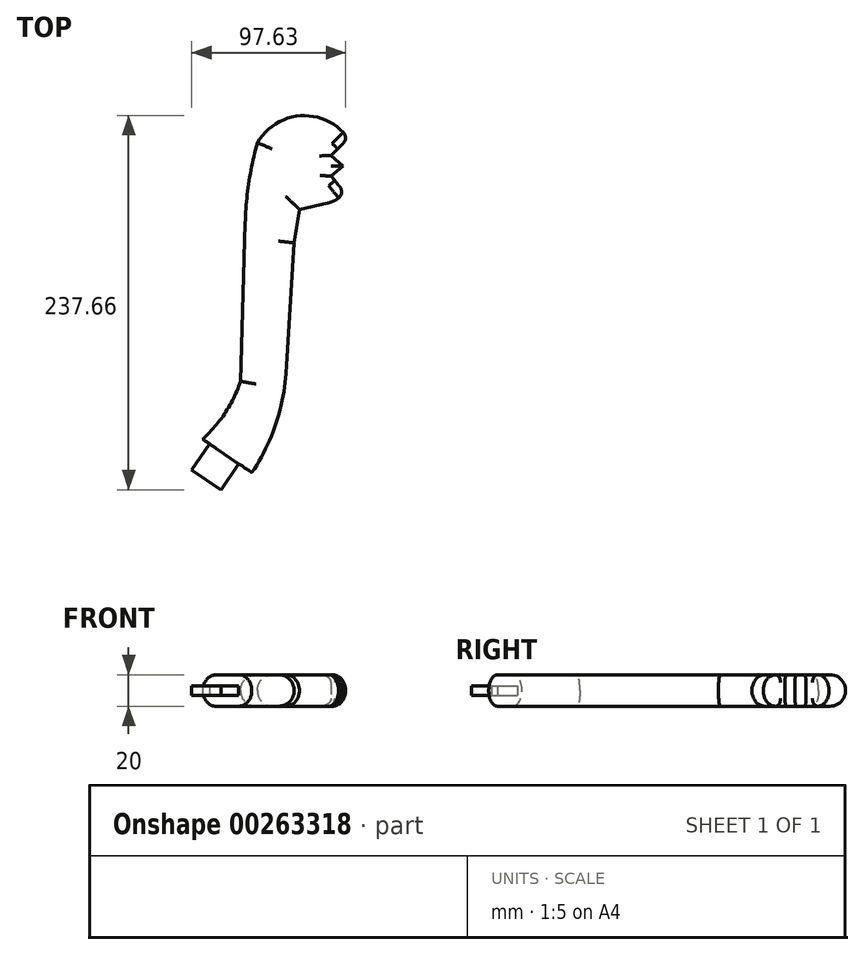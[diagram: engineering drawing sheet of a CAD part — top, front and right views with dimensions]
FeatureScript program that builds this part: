
annotation { "Feature Type Name" : "Feature", "Feature Type Description" : "" }
export const myFeature = defineFeature(function(context is Context, id is Id, definition is map)
    precondition{}
    {
        {
            var Q0;
            Q0=qCreatedBy(makeId("Top.planeOp"),FACE);
            var sketch = newSketch(context, id + "F0", { "sketchPlane" : qUnion([Q0])});
            skArc(sketch, "E0", {"start": v(-69.56, -48.3) * mm, "mid": v(-88.08, -45.25) * mm, "end": v(-106.8, -43.78) * mm});
            skArc(sketch, "E1", {"start": v(-106.8, -43.78) * mm, "mid": v(-96.39, -62.57) * mm, "end": v(-80.73, -77.27) * mm});
            skArc(sketch, "E2", {"start": v(-80.73, -77.27) * mm, "mid": v(-98.26, -84.7) * mm, "end": v(-114.23, -95.07) * mm});
            skArc(sketch, "E3", {"start": v(-114.23, -95.07) * mm, "mid": v(-98.6, -104.41) * mm, "end": v(-80.73, -107.98) * mm});
            skArc(sketch, "E4", {"start": v(-80.73, -107.98) * mm, "mid": v(-90.04, -123.58) * mm, "end": v(-94.69, -141.13) * mm});
            skArc(sketch, "E5", {"start": v(-94.69, -141.13) * mm, "mid": v(-78.8, -139.7) * mm, "end": v(-63.98, -133.8) * mm});
            skArc(sketch, "E6", {"start": v(-63.98, -133.8) * mm, "mid": v(40.14, -139.24) * mm, "end": v(30.94, -35.4) * mm});
            skArc(sketch, "E7", {"start": v(-31.41, -22.87) * mm, "mid": v(-53.17, -31.57) * mm, "end": v(-69.56, -48.3) * mm});
            skCircle(sketch, "E8", {"center": v(-12, -90) * mm, "radius": 35 * mm});
            skLineSegment(sketch, "E9", {"start": v(-12, -90) * mm, "end": v(-12, 0) * mm});
            skLineSegment(sketch, "E10", {"start": v(-12, 0) * mm, "end": v(0, 0) * mm});
            skLineSegment(sketch, "E11", {"start": v(-31.41, -22.87) * mm, "end": v(-12, 0) * mm});
            skLineSegment(sketch, "E12", {"start": v(-31.41, -22.87) * mm, "end": v(0, 0) * mm});
            skArc(sketch, "E13", {"start": v(30.94, -35.4) * mm, "mid": v(57.65, 8.29) * mm, "end": v(64.82, 58.99) * mm});
            skLineSegment(sketch, "E14", {"start": v(64.82, 42.9) * mm, "end": v(70.1, 125.75) * mm});
            skLineSegment(sketch, "E15", {"start": v(70.1, 125.75) * mm, "end": v(73.47, 146.99) * mm});
            skLineSegment(sketch, "E16", {"start": v(73.47, 146.99) * mm, "end": v(91.25, 150.97) * mm});
            skArc(sketch, "E17", {"start": v(93.55, 168.05) * mm, "mid": v(98.13, 170.3) * mm, "end": v(101.04, 174.5) * mm});
            skArc(sketch, "E18", {"start": v(101.04, 174.5) * mm, "mid": v(98.19, 178.86) * mm, "end": v(93.55, 181.22) * mm});
            skArc(sketch, "E19", {"start": v(91.25, 150.97) * mm, "mid": v(97.19, 153.5) * mm, "end": v(101.85, 157.96) * mm});
            skArc(sketch, "E20", {"start": v(101.85, 157.96) * mm, "mid": v(99.5, 164.5) * mm, "end": v(93.55, 168.05) * mm});
            skArc(sketch, "E21", {"start": v(93.55, 181.22) * mm, "mid": v(100.45, 185.24) * mm, "end": v(104.38, 192.2) * mm});
            skArc(sketch, "E22", {"start": v(16.27, 5.35) * mm, "mid": v(27.94, 20.47) * mm, "end": v(35.96, 37.8) * mm});
            skLineSegment(sketch, "E23", {"start": v(16.27, 5.35) * mm, "end": v(12.02, 0.97) * mm});
            skLineSegment(sketch, "E24", {"start": v(12.02, 54.47) * mm, "end": v(16.98, 220.58) * mm});
            skLineSegment(sketch, "E25", {"start": v(16.98, 220.58) * mm, "end": v(16.98, 230.48) * mm});
            skArc(sketch, "E26", {"start": v(20.74, 234.78) * mm, "mid": v(18.05, 233.34) * mm, "end": v(16.98, 230.48) * mm});
            skLineSegment(sketch, "E27", {"start": v(20.74, 234.78) * mm, "end": v(55.67, 234.78) * mm});
            skArc(sketch, "E28", {"start": v(55.67, 234.78) * mm, "mid": v(75.45, 242.82) * mm, "end": v(84, 262.38) * mm});
            skArc(sketch, "E29", {"start": v(84, 262.38) * mm, "mid": v(83.8, 275) * mm, "end": v(79.59, 286.9) * mm});
            skArc(sketch, "E30", {"start": v(79.59, 286.9) * mm, "mid": v(90.12, 305.47) * mm, "end": v(96.46, 325.87) * mm});
            skArc(sketch, "E31", {"start": v(96.46, 325.87) * mm, "mid": v(80.34, 314.22) * mm, "end": v(65.52, 300.95) * mm});
            skArc(sketch, "E32", {"start": v(65.52, 300.95) * mm, "mid": v(66.02, 314.82) * mm, "end": v(65.52, 328.68) * mm});
            skArc(sketch, "E33", {"start": v(41.86, 304.54) * mm, "mid": v(40.03, 315.53) * mm, "end": v(35.9, 325.87) * mm});
            skArc(sketch, "E34", {"start": v(35.9, 325.87) * mm, "mid": v(29.68, 316.4) * mm, "end": v(23.68, 306.81) * mm});
            skArc(sketch, "E35", {"start": v(23.68, 306.81) * mm, "mid": v(-21.12, 284.92) * mm, "end": v(-28, 235.53) * mm});
            skLineSegment(sketch, "E36", {"start": v(-31.41, -22.87) * mm, "end": v(-28, 235.53) * mm});
            skLineSegment(sketch, "E37", {"start": v(0, 0) * mm, "end": v(0, 302.13) * mm});
            skLineSegment(sketch, "E38", {"start": v(12.02, 0.97) * mm, "end": v(-31.41, -22.87) * mm});
            skLineSegment(sketch, "E39", {"start": v(0, 0) * mm, "end": v(12.02, 0.97) * mm});
            skLineSegment(sketch, "E40", {"start": v(12.02, 0.97) * mm, "end": v(30.94, -35.4) * mm});
            skLineSegment(sketch, "E41", {"start": v(64.82, 58.99) * mm, "end": v(46.6, 104.17) * mm});
            skLineSegment(sketch, "E42", {"start": v(12.02, 0.97) * mm, "end": v(12.02, 54.47) * mm});
            skLineSegment(sketch, "E43", {"start": v(-29.54, 119.27) * mm, "end": v(13.94, 118.7) * mm});
            skLineSegment(sketch, "E44", {"start": v(35.96, 37.8) * mm, "end": v(38.97, 138.47) * mm});
            skArc(sketch, "E45", {"start": v(104.38, 192.2) * mm, "mid": v(74.78, 206.52) * mm, "end": v(46.71, 189.39) * mm});
            skArc(sketch, "E46", {"start": v(46.71, 189.39) * mm, "mid": v(41.3, 164.16) * mm, "end": v(38.97, 138.47) * mm});
            skLineSegment(sketch, "E47", {"start": v(104.38, 192.2) * mm, "end": v(93.55, 181.22) * mm});
            skLineSegment(sketch, "E48", {"start": v(93.55, 168.05) * mm, "end": v(101.85, 157.96) * mm});
            skLineSegment(sketch, "E49", {"start": v(93.55, 181.22) * mm, "end": v(101.04, 174.5) * mm});
            skLineSegment(sketch, "E50", {"start": v(93.55, 168.05) * mm, "end": v(101.04, 174.5) * mm});
            skLineSegment(sketch, "E51", {"start": v(41.86, 304.54) * mm, "end": v(65.52, 328.68) * mm});
            skLineSegment(sketch, "E52", {"start": v(16.98, 230.48) * mm, "end": v(-28.07, 230.48) * mm});
            skLineSegment(sketch, "E53", {"start": v(12.02, 0.97) * mm, "end": v(-31.1, 0.49) * mm});
            skPoint(sketch, "E53.endSnap0", {"position": v(6.01, 0.49) * mm});
            skLineSegment(sketch, "E54", {"start": v(12.02, 0.97) * mm, "end": v(43.15, -20.17) * mm});
            skSolve(sketch);
        }
        {
            var Q0;
            {var subQ0=sQuery(id+"F0.wireOp",EDGE,"E38");var subQ1=sQuery(id+"F0.wireOp",EDGE,"E9");var subQ2=makeQuery(id+"F0.imprint","INTERSECT",VERTEX,{"derivedFrom":[subQ1,subQ0]});Q0=makeQuery(id+"F0.imprint","IMPRINT",FACE,{"disambiguationData":[TD([[makeQuery(id+"F0.imprint","IMPRINT",EDGE,{"disambiguationData":[TD([[subQ2,-1.0]])],"derivedFrom":subQ1}),1.0]])]});}
            var Q1;
            {var subQ0=sQuery(id+"F0.wireOp",EDGE,"E11");Q1=makeQuery(id+"F0.imprint","IMPRINT",FACE,{"disambiguationData":[TD([[makeQuery(id+"F0.imprint","IMPRINT",EDGE,{"derivedFrom":subQ0}),-1.0]])]});}
            var Q2;
            {var subQ0=sQuery(id+"F0.wireOp",EDGE,"E39");Q2=makeQuery(id+"F0.imprint","IMPRINT",FACE,{"disambiguationData":[TD([[makeQuery(id+"F0.imprint","IMPRINT",EDGE,{"derivedFrom":subQ0}),1.0]])]});}
            var Q3;
            Q3=makeQuery(id+"F0.imprint","IMPRINT",FACE,{"disambiguationData":[TD([[makeQuery(id+"F0.imprint","IMPRINT",EDGE,{"derivedFrom":sQuery(id+"F0.wireOp",EDGE,"E0")}),1.0]])]});
            var Q4;
            {var subQ5=sQuery(id+"F0.wireOp",EDGE,"E39");Q4=makeQuery(id+"F0.imprint","IMPRINT",FACE,{"disambiguationData":[TD([[makeQuery(id+"F0.imprint","IMPRINT",EDGE,{"derivedFrom":subQ5}),-1.0]])]});}
            var Q5;
            {var subQ2=sQuery(id+"F0.wireOp",EDGE,"E10");Q5=makeQuery(id+"F0.imprint","IMPRINT",FACE,{"disambiguationData":[TD([[makeQuery(id+"F0.imprint","IMPRINT",EDGE,{"derivedFrom":subQ2}),1.0]])]});}
            var Q6;
            {var subQ0=sQuery(id+"F0.wireOp",EDGE,"E10");Q6=makeQuery(id+"F0.imprint","IMPRINT",FACE,{"disambiguationData":[TD([[makeQuery(id+"F0.imprint","IMPRINT",EDGE,{"derivedFrom":subQ0}),-1.0]])]});}
            var Q7;
            {var subQ0=sQuery(id+"F0.wireOp",EDGE,"E40");Q7=makeQuery(id+"F0.imprint","IMPRINT",FACE,{"disambiguationData":[TD([[makeQuery(id+"F0.imprint","IMPRINT",EDGE,{"derivedFrom":subQ0}),1.0]])]});}
            extrude(context, id + "F1", {"entities" : qUnion([Q0, Q1, Q2, Q3, Q4, Q5, Q6, Q7]), "depth" : 20 * mm});
        }
        {
            var Q0;
            {var subQ1=sQuery(id+"F0.wireOp",EDGE,"E14");Q0=makeQuery(id+"F0.imprint","IMPRINT",FACE,{"disambiguationData":[TD([[makeQuery(id+"F0.imprint","IMPRINT",EDGE,{"derivedFrom":subQ1}),1.0]])]});}
            extrude(context, id + "F2", {"entities" : qUnion([Q0]), "depth" : 20 * mm});
        }
        {
            var Q0;
            {var subQ0=sQuery(id+"F0.wireOp",EDGE,"E43");var subQ1=sQuery(id+"F0.wireOp",EDGE,"E36");var subQ2=makeQuery(id+"F0.imprint","INTERSECT",VERTEX,{"derivedFrom":[subQ1,subQ0]});Q0=makeQuery(id+"F0.imprint","IMPRINT",FACE,{"disambiguationData":[TD([[makeQuery(id+"F0.imprint","IMPRINT",EDGE,{"disambiguationData":[TD([[subQ2,1.0]])],"derivedFrom":subQ1}),-1.0]])]});}
            var Q1;
            {var subQ5=sQuery(id+"F0.wireOp",EDGE,"E42");Q1=makeQuery(id+"F0.imprint","IMPRINT",FACE,{"disambiguationData":[TD([[makeQuery(id+"F0.imprint","IMPRINT",EDGE,{"derivedFrom":subQ5}),1.0]])]});}
            var Q2;
            {var subQ0=sQuery(id+"F0.wireOp",EDGE,"E43");var subQ1=sQuery(id+"F0.wireOp",EDGE,"E36");var subQ2=makeQuery(id+"F0.imprint","INTERSECT",VERTEX,{"derivedFrom":[subQ1,subQ0]});Q2=makeQuery(id+"F0.imprint","IMPRINT",FACE,{"disambiguationData":[TD([[makeQuery(id+"F0.imprint","IMPRINT",EDGE,{"disambiguationData":[TD([[subQ2,-1.0]])],"derivedFrom":subQ1}),-1.0]])]});}
            var Q3;
            {var subQ7=sQuery(id+"F0.wireOp",EDGE,"E25");Q3=makeQuery(id+"F0.imprint","IMPRINT",FACE,{"disambiguationData":[TD([[makeQuery(id+"F0.imprint","IMPRINT",EDGE,{"derivedFrom":subQ7}),1.0]])]});}
            extrude(context, id + "F3", {"entities" : qUnion([Q0, Q1, Q2, Q3]), "depth" : 20 * mm});
        }
        {
            var Q0;
            {var subQ0=sQuery(id+"F0.wireOp",EDGE,"E36");var subQ1=sQuery(id+"F0.wireOp",EDGE,"E35");var subQ2=makeQuery(id+"F0.imprint","INTERSECT",VERTEX,{"derivedFrom":[subQ1,subQ0]});Q0=makeQuery(id+"F0.imprint","IMPRINT",FACE,{"disambiguationData":[TD([[makeQuery(id+"F0.imprint","IMPRINT",EDGE,{"disambiguationData":[TD([[subQ2,1.0]])],"derivedFrom":subQ1}),1.0]])]});}
            var Q1;
            {var subQ4=sQuery(id+"F0.wireOp",EDGE,"E26");Q1=makeQuery(id+"F0.imprint","IMPRINT",FACE,{"disambiguationData":[TD([[makeQuery(id+"F0.imprint","IMPRINT",EDGE,{"derivedFrom":subQ4}),-1.0]])]});}
            extrude(context, id + "F4", {"entities" : qUnion([Q0, Q1]), "depth" : 20 * mm});
        }
        {
            var Q0;
            Q0=makeQuery(id+"F1.opExtrude","CAP_EDGE",EDGE,{"disambiguationData":[OSD([sQuery(id+"F0.wireOp",EDGE,"E36")])],"isStart":false});
            var Q1;
            Q1=makeQuery(id+"F1.opExtrude","CAP_EDGE",EDGE,{"disambiguationData":[OSD([sQuery(id+"F0.wireOp",EDGE,"E24")])],"isStart":false});
            var Q2;
            Q2=makeQuery(id+"F1.opExtrude","CAP_EDGE",EDGE,{"disambiguationData":[OSD([sQuery(id+"F0.wireOp",EDGE,"E42")])],"isStart":false});
            var Q3;
            Q3=makeQuery(id+"F1.opExtrude","CAP_EDGE",EDGE,{"disambiguationData":[OSD([sQuery(id+"F0.wireOp",EDGE,"E25")])],"isStart":false});
            var Q4;
            Q4=makeQuery(id+"F1.opExtrude","CAP_EDGE",EDGE,{"disambiguationData":[OSD([sQuery(id+"F0.wireOp",EDGE,"E35")])],"isStart":false});
            var Q5;
            Q5=makeQuery(id+"F1.opExtrude","CAP_EDGE",EDGE,{"disambiguationData":[OSD([sQuery(id+"F0.wireOp",EDGE,"E26")])],"isStart":false});
            var Q6;
            Q6=makeQuery(id+"F1.opExtrude","CAP_EDGE",EDGE,{"disambiguationData":[OSD([sQuery(id+"F0.wireOp",EDGE,"E42")])],"isStart":true});
            var Q7;
            Q7=makeQuery(id+"F1.opExtrude","CAP_EDGE",EDGE,{"disambiguationData":[OSD([sQuery(id+"F0.wireOp",EDGE,"E25")])],"isStart":true});
            var Q8;
            Q8=makeQuery(id+"F1.opExtrude","CAP_EDGE",EDGE,{"disambiguationData":[OSD([sQuery(id+"F0.wireOp",EDGE,"E36")])],"isStart":true});
            var Q9;
            Q9=makeQuery(id+"F1.opExtrude","CAP_EDGE",EDGE,{"disambiguationData":[OSD([sQuery(id+"F0.wireOp",EDGE,"E35")])],"isStart":true});
            var Q10;
            Q10=makeQuery(id+"F1.opExtrude","CAP_EDGE",EDGE,{"disambiguationData":[OSD([sQuery(id+"F0.wireOp",EDGE,"E26")])],"isStart":true});
            var Q11;
            Q11=makeQuery(id+"F1.opExtrude","CAP_EDGE",EDGE,{"disambiguationData":[OSD([sQuery(id+"F0.wireOp",EDGE,"E22")])],"isStart":false});
            var Q12;
            Q12=makeQuery(id+"F1.opExtrude","CAP_EDGE",EDGE,{"disambiguationData":[OSD([sQuery(id+"F0.wireOp",EDGE,"E23")])],"isStart":false});
            var Q13;
            Q13=makeQuery(id+"F1.opExtrude","CAP_EDGE",EDGE,{"disambiguationData":[OSD([sQuery(id+"F0.wireOp",EDGE,"E44")])],"isStart":false});
            var Q14;
            Q14=makeQuery(id+"F1.opExtrude","CAP_EDGE",EDGE,{"disambiguationData":[OSD([sQuery(id+"F0.wireOp",EDGE,"E45")])],"isStart":false});
            var Q15;
            Q15=makeQuery(id+"F1.opExtrude","CAP_EDGE",EDGE,{"disambiguationData":[OSD([sQuery(id+"F0.wireOp",EDGE,"E22")])],"isStart":true});
            var Q16;
            Q16=makeQuery(id+"F1.opExtrude","CAP_EDGE",EDGE,{"disambiguationData":[OSD([sQuery(id+"F0.wireOp",EDGE,"E44")])],"isStart":true});
            var Q17;
            Q17=makeQuery(id+"F1.opExtrude","CAP_EDGE",EDGE,{"disambiguationData":[OSD([sQuery(id+"F0.wireOp",EDGE,"E45")])],"isStart":true});
            var Q18;
            Q18=makeQuery(id+"F1.opExtrude","CAP_EDGE",EDGE,{"disambiguationData":[OSD([sQuery(id+"F0.wireOp",EDGE,"E13")])],"isStart":false});
            var Q19;
            Q19=makeQuery(id+"F1.opExtrude","CAP_EDGE",EDGE,{"disambiguationData":[OSD([sQuery(id+"F0.wireOp",EDGE,"E14")])],"isStart":false});
            var Q20;
            Q20=makeQuery(id+"F1.opExtrude","CAP_EDGE",EDGE,{"disambiguationData":[OSD([sQuery(id+"F0.wireOp",EDGE,"E15")])],"isStart":false});
            var Q21;
            Q21=makeQuery(id+"F1.opExtrude","CAP_EDGE",EDGE,{"disambiguationData":[OSD([sQuery(id+"F0.wireOp",EDGE,"E16")])],"isStart":false});
            var Q22;
            Q22=makeQuery(id+"F1.opExtrude","CAP_EDGE",EDGE,{"disambiguationData":[OSD([sQuery(id+"F0.wireOp",EDGE,"E16")])],"isStart":true});
            var Q23;
            Q23=makeQuery(id+"F1.opExtrude","CAP_EDGE",EDGE,{"disambiguationData":[OSD([sQuery(id+"F0.wireOp",EDGE,"E15")])],"isStart":true});
            var Q24;
            Q24=makeQuery(id+"F1.opExtrude","CAP_EDGE",EDGE,{"disambiguationData":[OSD([sQuery(id+"F0.wireOp",EDGE,"E14")])],"isStart":true});
            var Q25;
            Q25=makeQuery(id+"F1.opExtrude","CAP_EDGE",EDGE,{"disambiguationData":[OSD([sQuery(id+"F0.wireOp",EDGE,"E13")])],"isStart":true});
            var Q26;
            Q26=makeQuery(id+"F1.opExtrude","CAP_EDGE",EDGE,{"disambiguationData":[OSD([sQuery(id+"F0.wireOp",EDGE,"E6")])],"isStart":false});
            var Q27;
            Q27=makeQuery(id+"F1.opExtrude","CAP_EDGE",EDGE,{"disambiguationData":[OSD([sQuery(id+"F0.wireOp",EDGE,"E8")])],"isStart":false});
            var Q28;
            Q28=makeQuery(id+"F1.opExtrude","CAP_EDGE",EDGE,{"disambiguationData":[OSD([sQuery(id+"F0.wireOp",EDGE,"E7")])],"isStart":false});
            var Q29;
            Q29=makeQuery(id+"F1.opExtrude","CAP_EDGE",EDGE,{"disambiguationData":[OSD([sQuery(id+"F0.wireOp",EDGE,"E8")])],"isStart":true});
            var Q30;
            Q30=makeQuery(id+"F1.opExtrude","CAP_EDGE",EDGE,{"disambiguationData":[OSD([sQuery(id+"F0.wireOp",EDGE,"E7")])],"isStart":true});
            var Q31;
            Q31=makeQuery(id+"F1.opExtrude","CAP_EDGE",EDGE,{"disambiguationData":[OSD([sQuery(id+"F0.wireOp",EDGE,"E6")])],"isStart":true});
            fillet(context, id + "F5", {"entities" : qUnion([Q0, Q1, Q2, Q3, Q4, Q5, Q6, Q7, Q8, Q9, Q10, Q11, Q12, Q13, Q14, Q15, Q16, Q17, Q18, Q19, Q20, Q21, Q22, Q23, Q24, Q25, Q26, Q27, Q28, Q29, Q30, Q31]), "radius" : 10 * mm, "tangentPropagation" : true, "allowEdgeOverflow" : false});
        }
        {
            var Q0;
            Q0=makeQuery(id+"F1.opExtrude","CAP_EDGE",EDGE,{"disambiguationData":[OSD([sQuery(id+"F0.wireOp",EDGE,"E0")])],"isStart":false});
            var Q1;
            Q1=makeQuery(id+"F1.opExtrude","CAP_EDGE",EDGE,{"disambiguationData":[OSD([sQuery(id+"F0.wireOp",EDGE,"E1")])],"isStart":false});
            var Q2;
            Q2=makeQuery(id+"F1.opExtrude","CAP_EDGE",EDGE,{"disambiguationData":[OSD([sQuery(id+"F0.wireOp",EDGE,"E5")])],"isStart":false});
            var Q3;
            Q3=makeQuery(id+"F1.opExtrude","CAP_EDGE",EDGE,{"disambiguationData":[OSD([sQuery(id+"F0.wireOp",EDGE,"E4")])],"isStart":false});
            var Q4;
            Q4=makeQuery(id+"F1.opExtrude","CAP_EDGE",EDGE,{"disambiguationData":[OSD([sQuery(id+"F0.wireOp",EDGE,"E0")])],"isStart":true});
            var Q5;
            Q5=makeQuery(id+"F1.opExtrude","CAP_EDGE",EDGE,{"disambiguationData":[OSD([sQuery(id+"F0.wireOp",EDGE,"E1")])],"isStart":true});
            var Q6;
            Q6=makeQuery(id+"F1.opExtrude","CAP_EDGE",EDGE,{"disambiguationData":[OSD([sQuery(id+"F0.wireOp",EDGE,"E4")])],"isStart":true});
            var Q7;
            Q7=makeQuery(id+"F1.opExtrude","CAP_EDGE",EDGE,{"disambiguationData":[OSD([sQuery(id+"F0.wireOp",EDGE,"E5")])],"isStart":true});
            fillet(context, id + "F6", {"entities" : qUnion([Q0, Q1, Q2, Q3, Q4, Q5, Q6, Q7]), "radius" : 9.5 * mm, "tangentPropagation" : true, "rho" : 0.5, "crossSection" : FilletCrossSection.CONIC, "allowEdgeOverflow" : false});
        }
        {
            var Q0;
            Q0=makeQuery(id+"F1.opExtrude","CAP_EDGE",EDGE,{"disambiguationData":[OSD([sQuery(id+"F0.wireOp",EDGE,"E3")])],"isStart":true});
            var Q1;
            Q1=makeQuery(id+"F1.opExtrude","CAP_EDGE",EDGE,{"disambiguationData":[OSD([sQuery(id+"F0.wireOp",EDGE,"E2")])],"isStart":true});
            var Q2;
            Q2=makeQuery(id+"F1.opExtrude","CAP_EDGE",EDGE,{"disambiguationData":[OSD([sQuery(id+"F0.wireOp",EDGE,"E2")])],"isStart":false});
            var Q3;
            Q3=makeQuery(id+"F1.opExtrude","CAP_EDGE",EDGE,{"disambiguationData":[OSD([sQuery(id+"F0.wireOp",EDGE,"E3")])],"isStart":false});
            fillet(context, id + "F7", {"entities" : qUnion([Q0, Q1, Q2, Q3]), "radius" : 3 * mm, "tangentPropagation" : true, "allowEdgeOverflow" : false});
        }
        {
            var Q0;
            Q0=makeQuery(id+"F2.opExtrude","CAP_EDGE",EDGE,{"disambiguationData":[OSD([sQuery(id+"F0.wireOp",EDGE,"E14")])],"isStart":false});
            var Q1;
            Q1=makeQuery(id+"F2.opExtrude","CAP_EDGE",EDGE,{"disambiguationData":[OSD([sQuery(id+"F0.wireOp",EDGE,"E15")])],"isStart":false});
            var Q2;
            Q2=makeQuery(id+"F2.opExtrude","CAP_EDGE",EDGE,{"disambiguationData":[OSD([sQuery(id+"F0.wireOp",EDGE,"E14")])],"isStart":true});
            var Q3;
            Q3=makeQuery(id+"F2.opExtrude","CAP_EDGE",EDGE,{"disambiguationData":[OSD([sQuery(id+"F0.wireOp",EDGE,"E15")])],"isStart":true});
            var Q4;
            Q4=makeQuery(id+"F2.opExtrude","CAP_EDGE",EDGE,{"disambiguationData":[OSD([sQuery(id+"F0.wireOp",EDGE,"E16")])],"isStart":true});
            var Q5;
            Q5=makeQuery(id+"F2.opExtrude","CAP_EDGE",EDGE,{"disambiguationData":[OSD([sQuery(id+"F0.wireOp",EDGE,"E16")])],"isStart":false});
            var Q6;
            Q6=makeQuery(id+"F2.opExtrude","CAP_EDGE",EDGE,{"disambiguationData":[OSD([sQuery(id+"F0.wireOp",EDGE,"E45")])],"isStart":true});
            var Q7;
            Q7=makeQuery(id+"F2.opExtrude","CAP_EDGE",EDGE,{"disambiguationData":[OSD([sQuery(id+"F0.wireOp",EDGE,"E45")])],"isStart":false});
            var Q8;
            Q8=makeQuery(id+"F2.opExtrude","CAP_EDGE",EDGE,{"disambiguationData":[OSD([sQuery(id+"F0.wireOp",EDGE,"E46")])],"isStart":false});
            var Q9;
            Q9=makeQuery(id+"F2.opExtrude","CAP_EDGE",EDGE,{"disambiguationData":[OSD([sQuery(id+"F0.wireOp",EDGE,"E44")])],"isStart":false});
            var Q10;
            Q10=makeQuery(id+"F2.opExtrude","CAP_EDGE",EDGE,{"disambiguationData":[OSD([sQuery(id+"F0.wireOp",EDGE,"E22")])],"isStart":false});
            var Q11;
            Q11=makeQuery(id+"F2.opExtrude","CAP_EDGE",EDGE,{"disambiguationData":[OSD([sQuery(id+"F0.wireOp",EDGE,"E23")])],"isStart":false});
            var Q12;
            Q12=makeQuery(id+"F2.opExtrude","CAP_EDGE",EDGE,{"disambiguationData":[OSD([sQuery(id+"F0.wireOp",EDGE,"E46")])],"isStart":true});
            var Q13;
            Q13=makeQuery(id+"F2.opExtrude","CAP_EDGE",EDGE,{"disambiguationData":[OSD([sQuery(id+"F0.wireOp",EDGE,"E23")])],"isStart":true});
            var Q14;
            Q14=makeQuery(id+"F2.opExtrude","CAP_EDGE",EDGE,{"disambiguationData":[OSD([sQuery(id+"F0.wireOp",EDGE,"E22")])],"isStart":true});
            var Q15;
            Q15=makeQuery(id+"F2.opExtrude","CAP_EDGE",EDGE,{"disambiguationData":[OSD([sQuery(id+"F0.wireOp",EDGE,"E44")])],"isStart":true});
            var Q16;
            Q16=makeQuery(id+"F3.opExtrude","CAP_EDGE",EDGE,{"disambiguationData":[OSD([sQuery(id+"F0.wireOp",EDGE,"E24")])],"isStart":false});
            var Q17;
            Q17=makeQuery(id+"F3.opExtrude","CAP_EDGE",EDGE,{"disambiguationData":[OSD([sQuery(id+"F0.wireOp",EDGE,"E42")])],"isStart":false});
            var Q18;
            Q18=makeQuery(id+"F3.opExtrude","CAP_EDGE",EDGE,{"disambiguationData":[OSD([sQuery(id+"F0.wireOp",EDGE,"E42")])],"isStart":true});
            var Q19;
            Q19=makeQuery(id+"F3.opExtrude","CAP_EDGE",EDGE,{"disambiguationData":[OSD([sQuery(id+"F0.wireOp",EDGE,"E24")])],"isStart":true});
            var Q20;
            Q20=makeQuery(id+"F3.opExtrude","CAP_EDGE",EDGE,{"disambiguationData":[OSD([sQuery(id+"F0.wireOp",EDGE,"E25")])],"isStart":true});
            var Q21;
            Q21=makeQuery(id+"F3.opExtrude","CAP_EDGE",EDGE,{"disambiguationData":[OSD([sQuery(id+"F0.wireOp",EDGE,"E36")])],"isStart":false});
            var Q22;
            Q22=makeQuery(id+"F3.opExtrude","CAP_EDGE",EDGE,{"disambiguationData":[OSD([sQuery(id+"F0.wireOp",EDGE,"E36")])],"isStart":true});
            var Q23;
            Q23=makeQuery(id+"F4.opExtrude","CAP_EDGE",EDGE,{"disambiguationData":[OSD([sQuery(id+"F0.wireOp",EDGE,"E36")])],"isStart":true});
            var Q24;
            Q24=makeQuery(id+"F4.opExtrude","CAP_EDGE",EDGE,{"disambiguationData":[OSD([sQuery(id+"F0.wireOp",EDGE,"E36")])],"isStart":false});
            var Q25;
            Q25=makeQuery(id+"F4.opExtrude","CAP_EDGE",EDGE,{"disambiguationData":[OSD([sQuery(id+"F0.wireOp",EDGE,"E35")])],"isStart":true});
            var Q26;
            Q26=makeQuery(id+"F4.opExtrude","CAP_EDGE",EDGE,{"disambiguationData":[OSD([sQuery(id+"F0.wireOp",EDGE,"E35")])],"isStart":false});
            var Q27;
            Q27=makeQuery(id+"F4.opExtrude","CAP_EDGE",EDGE,{"disambiguationData":[OSD([sQuery(id+"F0.wireOp",EDGE,"E27")])],"isStart":false});
            var Q28;
            Q28=makeQuery(id+"F4.opExtrude","CAP_EDGE",EDGE,{"disambiguationData":[OSD([sQuery(id+"F0.wireOp",EDGE,"E28")])],"isStart":false});
            var Q29;
            Q29=makeQuery(id+"F4.opExtrude","CAP_EDGE",EDGE,{"disambiguationData":[OSD([sQuery(id+"F0.wireOp",EDGE,"E29")])],"isStart":false});
            var Q30;
            Q30=makeQuery(id+"F4.opExtrude","CAP_EDGE",EDGE,{"disambiguationData":[OSD([sQuery(id+"F0.wireOp",EDGE,"E27")])],"isStart":true});
            var Q31;
            Q31=makeQuery(id+"F4.opExtrude","CAP_EDGE",EDGE,{"disambiguationData":[OSD([sQuery(id+"F0.wireOp",EDGE,"E28")])],"isStart":true});
            var Q32;
            Q32=makeQuery(id+"F4.opExtrude","CAP_EDGE",EDGE,{"disambiguationData":[OSD([sQuery(id+"F0.wireOp",EDGE,"E29")])],"isStart":true});
            var Q33;
            Q33=makeQuery(id+"F4.opExtrude","CAP_EDGE",EDGE,{"disambiguationData":[OSD([sQuery(id+"F0.wireOp",EDGE,"E26")])],"isStart":false});
            var Q34;
            Q34=makeQuery(id+"F4.opExtrude","CAP_EDGE",EDGE,{"disambiguationData":[OSD([sQuery(id+"F0.wireOp",EDGE,"E26")])],"isStart":true});
            var Q35;
            Q35=makeQuery(id+"F4.opExtrude","CAP_EDGE",EDGE,{"disambiguationData":[OSD([sQuery(id+"F0.wireOp",EDGE,"E30")])],"isStart":false});
            var Q36;
            Q36=makeQuery(id+"F4.opExtrude","CAP_EDGE",EDGE,{"disambiguationData":[OSD([sQuery(id+"F0.wireOp",EDGE,"E31")])],"isStart":false});
            var Q37;
            Q37=makeQuery(id+"F4.opExtrude","CAP_EDGE",EDGE,{"disambiguationData":[OSD([sQuery(id+"F0.wireOp",EDGE,"E30")])],"isStart":true});
            var Q38;
            Q38=makeQuery(id+"F4.opExtrude","CAP_EDGE",EDGE,{"disambiguationData":[OSD([sQuery(id+"F0.wireOp",EDGE,"E31")])],"isStart":true});
            var Q39;
            Q39=makeQuery(id+"F4.opExtrude","CAP_EDGE",EDGE,{"disambiguationData":[OSD([sQuery(id+"F0.wireOp",EDGE,"E33")])],"isStart":false});
            var Q40;
            Q40=makeQuery(id+"F4.opExtrude","CAP_EDGE",EDGE,{"disambiguationData":[OSD([sQuery(id+"F0.wireOp",EDGE,"E34")])],"isStart":false});
            var Q41;
            Q41=makeQuery(id+"F4.opExtrude","CAP_EDGE",EDGE,{"disambiguationData":[OSD([sQuery(id+"F0.wireOp",EDGE,"E34")])],"isStart":true});
            var Q42;
            Q42=makeQuery(id+"F4.opExtrude","CAP_EDGE",EDGE,{"disambiguationData":[OSD([sQuery(id+"F0.wireOp",EDGE,"E33")])],"isStart":true});
            fillet(context, id + "F8", {"entities" : qUnion([Q0, Q1, Q2, Q3, Q4, Q5, Q6, Q7, Q8, Q9, Q10, Q11, Q12, Q13, Q14, Q15, Q16, Q17, Q18, Q19, Q20, Q21, Q22, Q23, Q24, Q25, Q26, Q27, Q28, Q29, Q30, Q31, Q32, Q33, Q34, Q35, Q36, Q37, Q38, Q39, Q40, Q41, Q42]), "radius" : 10 * mm, "tangentPropagation" : true, "allowEdgeOverflow" : false});
        }
        {
            var Q0;
            Q0=makeQuery(id+"F4.opExtrude","CAP_EDGE",EDGE,{"disambiguationData":[OSD([sQuery(id+"F0.wireOp",EDGE,"E51")])],"isStart":false});
            var Q1;
            Q1=makeQuery(id+"F4.opExtrude","CAP_EDGE",EDGE,{"disambiguationData":[OSD([sQuery(id+"F0.wireOp",EDGE,"E32")])],"isStart":false});
            var Q2;
            Q2=makeQuery(id+"F4.opExtrude","CAP_EDGE",EDGE,{"disambiguationData":[OSD([sQuery(id+"F0.wireOp",EDGE,"E32")])],"isStart":true});
            var Q3;
            Q3=makeQuery(id+"F4.opExtrude","CAP_EDGE",EDGE,{"disambiguationData":[OSD([sQuery(id+"F0.wireOp",EDGE,"E51")])],"isStart":true});
            fillet(context, id + "F9", {"entities" : qUnion([Q0, Q1, Q2, Q3]), "radius" : 5 * mm, "tangentPropagation" : true, "allowEdgeOverflow" : false});
        }
        {
            var Q0;
            Q0=makeQuery(id+"F2.opExtrude","CAP_EDGE",EDGE,{"disambiguationData":[OSD([sQuery(id+"F0.wireOp",EDGE,"E50")])],"isStart":true});
            var Q1;
            Q1=makeQuery(id+"F2.opExtrude","CAP_EDGE",EDGE,{"disambiguationData":[OSD([sQuery(id+"F0.wireOp",EDGE,"E49")])],"isStart":true});
            var Q2;
            Q2=makeQuery(id+"F2.opExtrude","CAP_EDGE",EDGE,{"disambiguationData":[OSD([sQuery(id+"F0.wireOp",EDGE,"E49")])],"isStart":false});
            var Q3;
            Q3=makeQuery(id+"F2.opExtrude","CAP_EDGE",EDGE,{"disambiguationData":[OSD([sQuery(id+"F0.wireOp",EDGE,"E50")])],"isStart":false});
            var Q4;
            Q4=makeQuery(id+"F8.opFillet","BLEND_EDGE",EDGE,{"blendedFrom":[makeQuery(id+"F2.opExtrude","CAP_EDGE",EDGE,{"disambiguationData":[OSD([sQuery(id+"F0.wireOp",EDGE,"E45")])],"isStart":false}),makeQuery(id+"F2.opExtrude","SWEPT_FACE",FACE,{"disambiguationData":[OSD([sQuery(id+"F0.wireOp",EDGE,"E47")])]})],"blendedInto":[makeQuery(id+"F2.opExtrude","SWEPT_FACE",FACE,{"disambiguationData":[OSD([sQuery(id+"F0.wireOp",EDGE,"E47")])]})]});
            var Q5;
            Q5=makeQuery(id+"F8.opFillet","BLEND_EDGE",EDGE,{"blendedFrom":[makeQuery(id+"F2.opExtrude","CAP_EDGE",EDGE,{"disambiguationData":[OSD([sQuery(id+"F0.wireOp",EDGE,"E19")])],"isStart":false}),makeQuery(id+"F2.opExtrude","SWEPT_FACE",FACE,{"disambiguationData":[OSD([sQuery(id+"F0.wireOp",EDGE,"E48")])]})],"blendedInto":[makeQuery(id+"F2.opExtrude","SWEPT_FACE",FACE,{"disambiguationData":[OSD([sQuery(id+"F0.wireOp",EDGE,"E48")])]})]});
            fillet(context, id + "F10", {"entities" : qUnion([Q0, Q1, Q2, Q3, Q4, Q5]), "radius" : 5 * mm, "tangentPropagation" : true, "allowEdgeOverflow" : false});
        }
        {
            var Q0;
            Q0=makeQuery(id+"F5.opFillet","SPLIT",FACE,{"disambiguationData":[OD(0.0)],"derivedFrom":makeQuery(id+"F1.opExtrude","CAP_FACE",FACE,{"disambiguationData":[OSD([sQuery(id+"F0.wireOp",EDGE,"E0"),sQuery(id+"F0.wireOp",EDGE,"E1"),sQuery(id+"F0.wireOp",EDGE,"E2"),sQuery(id+"F0.wireOp",EDGE,"E3"),sQuery(id+"F0.wireOp",EDGE,"E4"),sQuery(id+"F0.wireOp",EDGE,"E5"),sQuery(id+"F0.wireOp",EDGE,"E6"),sQuery(id+"F0.wireOp",EDGE,"E7"),sQuery(id+"F0.wireOp",EDGE,"E8"),sQuery(id+"F0.wireOp",EDGE,"E13"),sQuery(id+"F0.wireOp",EDGE,"E14"),sQuery(id+"F0.wireOp",EDGE,"E15"),sQuery(id+"F0.wireOp",EDGE,"E16"),sQuery(id+"F0.wireOp",EDGE,"E19"),sQuery(id+"F0.wireOp",EDGE,"E22"),sQuery(id+"F0.wireOp",EDGE,"E23"),sQuery(id+"F0.wireOp",EDGE,"E24"),sQuery(id+"F0.wireOp",EDGE,"E25"),sQuery(id+"F0.wireOp",EDGE,"E26"),sQuery(id+"F0.wireOp",EDGE,"E27"),sQuery(id+"F0.wireOp",EDGE,"E28"),sQuery(id+"F0.wireOp",EDGE,"E29"),sQuery(id+"F0.wireOp",EDGE,"E30"),sQuery(id+"F0.wireOp",EDGE,"E31"),sQuery(id+"F0.wireOp",EDGE,"E32"),sQuery(id+"F0.wireOp",EDGE,"E33"),sQuery(id+"F0.wireOp",EDGE,"E34"),sQuery(id+"F0.wireOp",EDGE,"E35"),sQuery(id+"F0.wireOp",EDGE,"E36"),sQuery(id+"F0.wireOp",EDGE,"E42"),sQuery(id+"F0.wireOp",EDGE,"E44"),sQuery(id+"F0.wireOp",EDGE,"E45"),sQuery(id+"F0.wireOp",EDGE,"E46"),sQuery(id+"F0.wireOp",EDGE,"E47"),sQuery(id+"F0.wireOp",EDGE,"E48"),sQuery(id+"F0.wireOp",EDGE,"E49"),sQuery(id+"F0.wireOp",EDGE,"E50"),sQuery(id+"F0.wireOp",EDGE,"E51")])],"isStart":false})});
            var sketch = newSketch(context, id + "F11", { "sketchPlane" : qUnion([Q0])});
            skLineSegment(sketch, "E55", {"start": v(0, 0) * mm, "end": v(3.83, 289.97) * mm});
            skLineSegment(sketch, "E56", {"start": v(3.83, 289.97) * mm, "end": v(19.83, 289.76) * mm});
            skCircle(sketch, "E57", {"center": v(19.83, 289.76) * mm, "radius": 10 * mm});
            skSolve(sketch);
        }
        {
            var Q0;
            Q0=makeQuery(id+"F11.imprint","IMPRINT",FACE,{"disambiguationData":[TD([[makeQuery(id+"F11.imprint","IMPRINT",EDGE,{"derivedFrom":sQuery(id+"F11.wireOp",EDGE,"E57")}),1.0]])]});
            extrude(context, id + "F12", {"entities" : qUnion([Q0]), "operationType" : NewBodyOperationType.ADD, "depth" : 5 * mm, "hasSecondDirection" : true, "secondDirectionOppositeDirection" : true, "secondDirectionDepth" : 25 * mm});
        }
        {
            var Q0;
            Q0=makeQuery(id+"F12.opExtrude","CAP_EDGE",EDGE,{"disambiguationData":[OSD([sQuery(id+"F11.wireOp",EDGE,"E57")])],"isStart":false});
            chamfer(context, id + "F13", {"entities" : qUnion([Q0]), "chamferType" : ChamferType.OFFSET_ANGLE, "width" : 7 * mm, "oppositeDirection" : false, "angle" : 30 * degree, "tangentPropagation" : true});
        }
        {
            var Q0;
            Q0=makeQuery(id+"F12.opExtrude","CAP_EDGE",EDGE,{"disambiguationData":[OSD([sQuery(id+"F11.wireOp",EDGE,"E57")])],"isStart":true});
            chamfer(context, id + "F14", {"entities" : qUnion([Q0]), "chamferType" : ChamferType.OFFSET_ANGLE, "width" : 4 * mm, "oppositeDirection" : false, "angle" : 60 * degree, "tangentPropagation" : true});
        }
        {
            var Q0;
            Q0=makeQuery(id+"F1.opExtrude","SWEPT_BODY",BODY,{"disambiguationData":[OSD([sQuery(id+"F0.wireOp",EDGE,"E0"),sQuery(id+"F0.wireOp",EDGE,"E1"),sQuery(id+"F0.wireOp",EDGE,"E2"),sQuery(id+"F0.wireOp",EDGE,"E3"),sQuery(id+"F0.wireOp",EDGE,"E4"),sQuery(id+"F0.wireOp",EDGE,"E5"),sQuery(id+"F0.wireOp",EDGE,"E6"),sQuery(id+"F0.wireOp",EDGE,"E7"),sQuery(id+"F0.wireOp",EDGE,"E8"),sQuery(id+"F0.wireOp",EDGE,"E13"),sQuery(id+"F0.wireOp",EDGE,"E36"),sQuery(id+"F0.wireOp",EDGE,"E53"),sQuery(id+"F0.wireOp",EDGE,"E54")])]});
            var Q1;
            Q1=makeQuery(id+"F3.opExtrude","SWEPT_BODY",BODY,{"disambiguationData":[OSD([sQuery(id+"F0.wireOp",EDGE,"E24"),sQuery(id+"F0.wireOp",EDGE,"E25"),sQuery(id+"F0.wireOp",EDGE,"E36"),sQuery(id+"F0.wireOp",EDGE,"E42"),sQuery(id+"F0.wireOp",EDGE,"E52"),sQuery(id+"F0.wireOp",EDGE,"E53")])]});
            deleteBodies(context, id + "F15", {"entities" : qUnion([Q0, Q1])});
        }
        {
            var Q0;
            Q0=makeQuery(id+"F4.opExtrude","SWEPT_BODY",BODY,{"disambiguationData":[OSD([sQuery(id+"F0.wireOp",EDGE,"E26"),sQuery(id+"F0.wireOp",EDGE,"E27"),sQuery(id+"F0.wireOp",EDGE,"E28"),sQuery(id+"F0.wireOp",EDGE,"E29"),sQuery(id+"F0.wireOp",EDGE,"E30"),sQuery(id+"F0.wireOp",EDGE,"E31"),sQuery(id+"F0.wireOp",EDGE,"E32"),sQuery(id+"F0.wireOp",EDGE,"E33"),sQuery(id+"F0.wireOp",EDGE,"E34"),sQuery(id+"F0.wireOp",EDGE,"E35"),sQuery(id+"F0.wireOp",EDGE,"E36"),sQuery(id+"F0.wireOp",EDGE,"E51"),sQuery(id+"F0.wireOp",EDGE,"E52")])]});
            deleteBodies(context, id + "F16", {"entities" : qUnion([Q0])});
        }
        {
            var Q0;
            Q0=makeQuery(id+"F2.opExtrude","SWEPT_FACE",FACE,{"disambiguationData":[OSD([sQuery(id+"F0.wireOp",EDGE,"E54")])]});
            var sketch = newSketch(context, id + "F17", { "sketchPlane" : qUnion([Q0])});
            skLineSegment(sketch, "E58", {"start": v(47.03, 10) * mm, "end": v(37.03, 10) * mm});
            skLineSegment(sketch, "E59", {"start": v(37.03, 10) * mm, "end": v(37.03, 13) * mm});
            skLineSegment(sketch, "E60.bottom", {"start": v(37.03, 13) * mm, "end": v(14.53, 13) * mm});
            skLineSegment(sketch, "E60.top", {"start": v(37.03, 7) * mm, "end": v(14.53, 7) * mm});
            skLineSegment(sketch, "E60.left", {"start": v(37.03, 13) * mm, "end": v(37.03, 7) * mm});
            skLineSegment(sketch, "E60.right", {"start": v(14.53, 13) * mm, "end": v(14.53, 7) * mm});
            skSolve(sketch);
        }
        {
            var Q0;
            Q0 = qSketchRegion(id + "F17", true);
            extrude(context, id + "F18", {"entities" : qUnion([Q0]), "operationType" : NewBodyOperationType.ADD, "depth" : 20 * mm});
        }
    });
